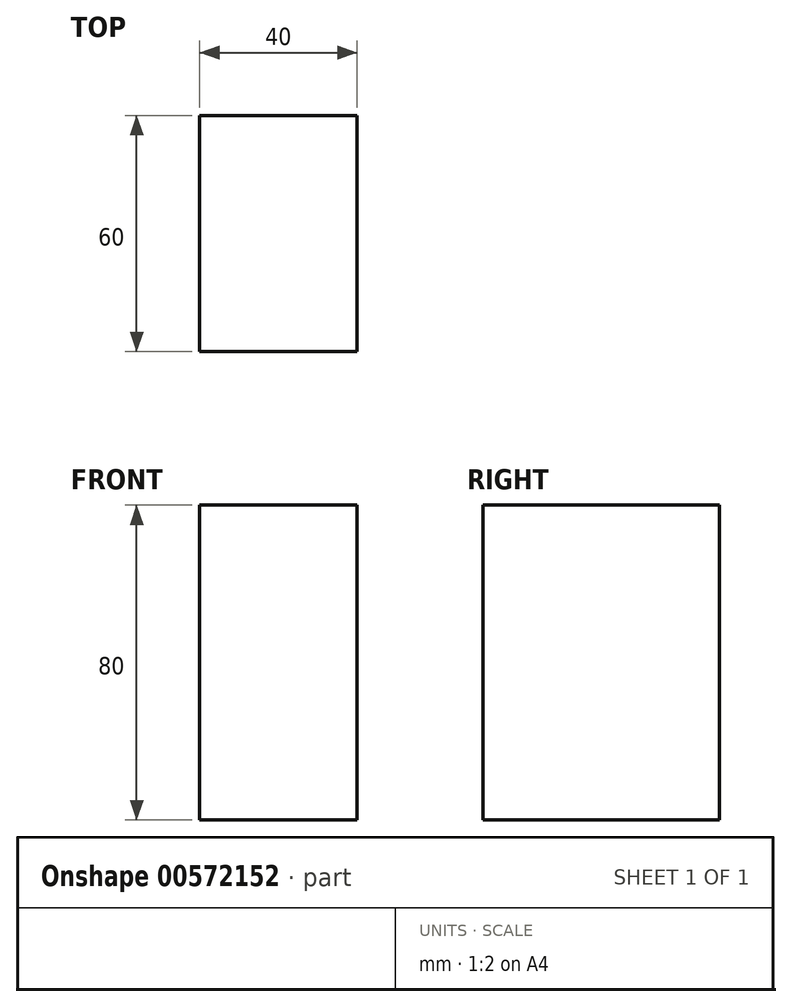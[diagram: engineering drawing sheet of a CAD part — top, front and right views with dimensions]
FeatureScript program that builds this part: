
annotation { "Feature Type Name" : "Feature", "Feature Type Description" : "" }
export const myFeature = defineFeature(function(context is Context, id is Id, definition is map)
    precondition{}
    {
        {
            var Q0;
            Q0=qCreatedBy(makeId("Top.planeOp"),FACE);
            var sketch = newSketch(context, id + "F0", { "sketchPlane" : qUnion([Q0])});
            skLineSegment(sketch, "E0.bottom", {"start": v(-35.4, 53.48) * mm, "end": v(4.6, 53.48) * mm});
            skLineSegment(sketch, "E0.top", {"start": v(-35.4, -6.52) * mm, "end": v(4.6, -6.52) * mm});
            skLineSegment(sketch, "E0.left", {"start": v(-35.4, 53.48) * mm, "end": v(-35.4, -6.52) * mm});
            skLineSegment(sketch, "E0.right", {"start": v(4.6, 53.48) * mm, "end": v(4.6, -6.52) * mm});
            skSolve(sketch);
        }
        {
            var Q0;
            Q0 = qSketchRegion(id + "F0", true);
            extrude(context, id + "F1", {"entities" : qUnion([Q0]), "depth" : 80 * mm, "offsetDistance" : 25 * mm});
        }
    });
